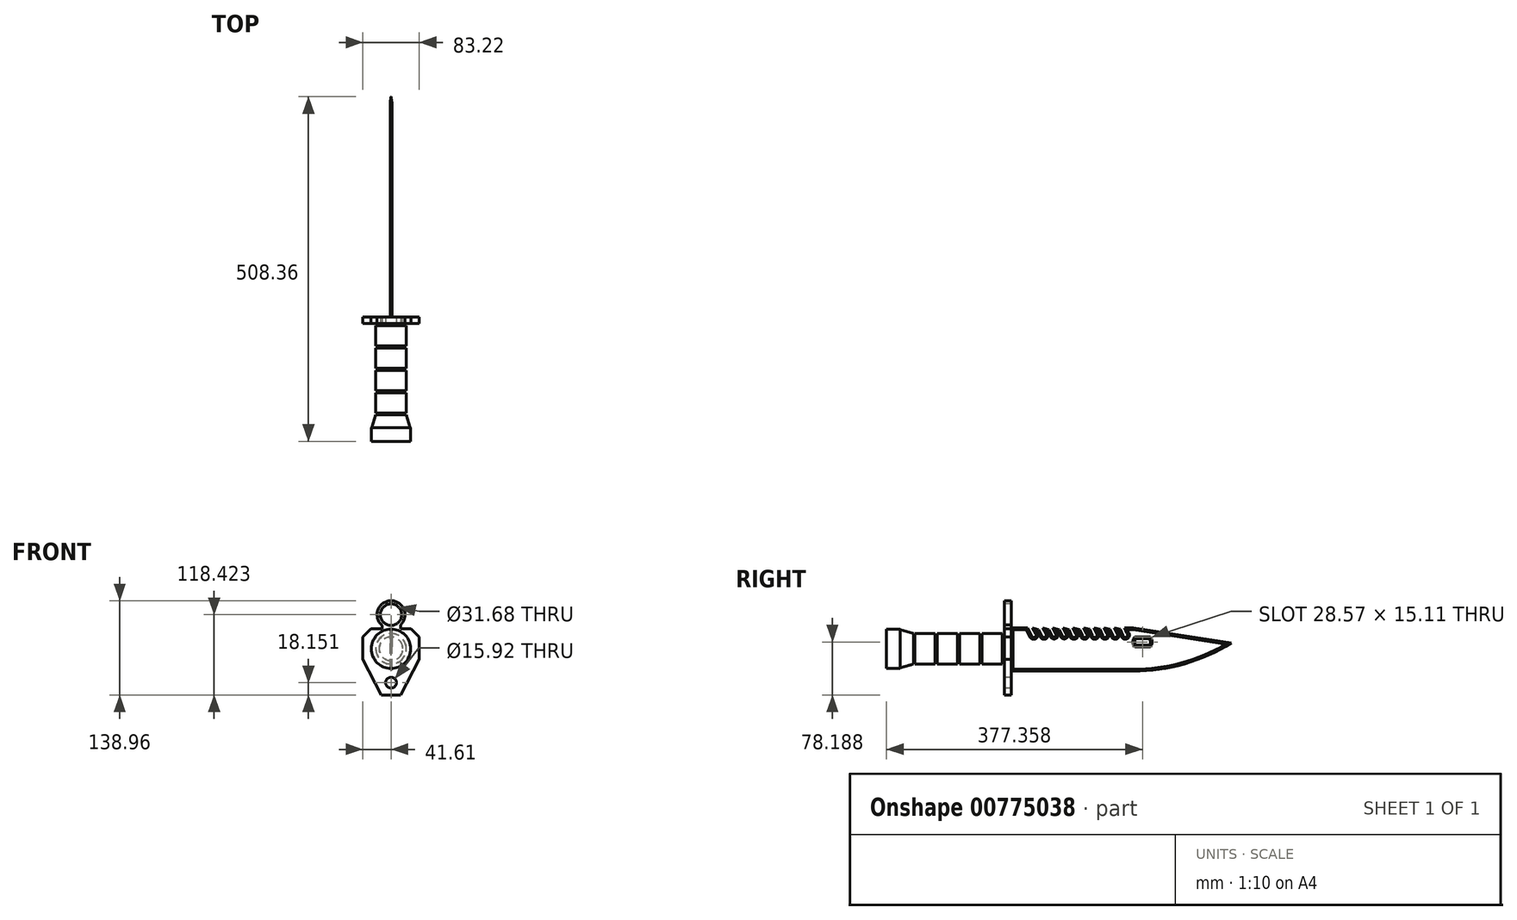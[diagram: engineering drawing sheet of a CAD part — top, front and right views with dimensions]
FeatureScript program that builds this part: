
annotation { "Feature Type Name" : "Feature", "Feature Type Description" : "" }
export const myFeature = defineFeature(function(context is Context, id is Id, definition is map)
    precondition{}
    {
        {
            var Q0;
            Q0=qCreatedBy(makeId("Right.planeOp"),FACE);
            var sketch = newSketch(context, id + "F0", { "sketchPlane" : qUnion([Q0])});
            skLineSegment(sketch, "E0", {"start": v(0, 0) * mm, "end": v(0, 17.36) * mm});
            skLineSegment(sketch, "E1", {"start": v(0, 17.36) * mm, "end": v(-3, 17.36) * mm});
            skLineSegment(sketch, "E2", {"start": v(-3, 17.36) * mm, "end": v(-3, 22.36) * mm});
            skLineSegment(sketch, "E3", {"start": v(-3, 22.36) * mm, "end": v(-33, 22.36) * mm});
            skLineSegment(sketch, "E4", {"start": v(-33, 22.36) * mm, "end": v(-33, 17.36) * mm});
            skLineSegment(sketch, "E5", {"start": v(-33, 17.36) * mm, "end": v(-36, 17.36) * mm});
            skLineSegment(sketch, "E6", {"start": v(-36, 17.36) * mm, "end": v(-36, 22.36) * mm});
            skLineSegment(sketch, "E7", {"start": v(-36, 22.36) * mm, "end": v(-66, 22.36) * mm});
            skLineSegment(sketch, "E8", {"start": v(-66, 22.36) * mm, "end": v(-66, 17.36) * mm});
            skLineSegment(sketch, "E9", {"start": v(-66, 17.36) * mm, "end": v(-69, 17.36) * mm});
            skLineSegment(sketch, "E10", {"start": v(-69, 17.36) * mm, "end": v(-69, 22.36) * mm});
            skLineSegment(sketch, "E11", {"start": v(-69, 22.36) * mm, "end": v(-99, 22.36) * mm});
            skLineSegment(sketch, "E12", {"start": v(-99, 22.36) * mm, "end": v(-99, 17.36) * mm});
            skLineSegment(sketch, "E13", {"start": v(-99, 17.36) * mm, "end": v(-102, 17.36) * mm});
            skLineSegment(sketch, "E14", {"start": v(-102, 17.36) * mm, "end": v(-102, 22.36) * mm});
            skLineSegment(sketch, "E15", {"start": v(-102, 22.36) * mm, "end": v(-132, 22.36) * mm});
            skLineSegment(sketch, "E16", {"start": v(-132, 22.36) * mm, "end": v(-132, 17.64) * mm});
            skLineSegment(sketch, "E17", {"start": v(-132, 17.64) * mm, "end": v(-134, 17.64) * mm});
            skLineSegment(sketch, "E18", {"start": v(-134, 17.64) * mm, "end": v(-134, 22.64) * mm});
            skLineSegment(sketch, "E19", {"start": v(-134, 22.64) * mm, "end": v(-153.56, 28.06) * mm});
            skLineSegment(sketch, "E20", {"start": v(-153.56, 28.06) * mm, "end": v(-153.56, 29.06) * mm});
            skLineSegment(sketch, "E21", {"start": v(-153.56, 29.06) * mm, "end": v(-173.56, 29.06) * mm});
            skLineSegment(sketch, "E22", {"start": v(-173.56, 29.06) * mm, "end": v(-173.56, 0) * mm});
            skLineSegment(sketch, "E23", {"start": v(-173.56, 0) * mm, "end": v(0, 0) * mm});
            skSolve(sketch);
        }
        {
            var Q0;
            Q0=qSketchRegion(id+"F0",true);
            var Q1;
            Q1=sQuery(id+"F0.wireOp",EDGE,"E23");
            revolve(context, id + "F1", {"entities" : qUnion([Q0]), "axis" : qUnion([Q1]), "revolveType" : RevolveType.FULL});
        }
        {
            var Q0;
            Q0=qCreatedBy(makeId("Front.planeOp"),FACE);
            var sketch = newSketch(context, id + "F2", { "sketchPlane" : qUnion([Q0])});
            skLineSegment(sketch, "E24", {"start": v(0, -68.1) * mm, "end": v(14.11, -68.1) * mm});
            skLineSegment(sketch, "E25", {"start": v(14.11, -68.1) * mm, "end": v(41.6, -15.3) * mm});
            skLineSegment(sketch, "E26", {"start": v(41.6, -15.3) * mm, "end": v(41.6, 17.5) * mm});
            skLineSegment(sketch, "E27", {"start": v(0, 29.79) * mm, "end": v(29.7, 29.79) * mm});
            skLineSegment(sketch, "E28", {"start": v(29.7, 29.79) * mm, "end": v(41.6, 17.5) * mm});
            skLineSegment(sketch, "E29.MirrorCS", {"start": v(-41.6, -15.3) * mm, "end": v(-41.6, 17.5) * mm});
            skLineSegment(sketch, "E30.MirrorCS", {"start": v(0, 29.79) * mm, "end": v(-29.7, 29.79) * mm});
            skLineSegment(sketch, "E31.MirrorCS", {"start": v(0, -68.1) * mm, "end": v(-14.11, -68.1) * mm});
            skLineSegment(sketch, "E32.MirrorCS", {"start": v(-14.11, -68.1) * mm, "end": v(-41.6, -15.3) * mm});
            skLineSegment(sketch, "E33.MirrorCS", {"start": v(-29.7, 29.79) * mm, "end": v(-41.6, 17.5) * mm});
            skCircle(sketch, "E34", {"center": v(0, -49.95) * mm, "radius": 7.96 * mm});
            skCircle(sketch, "E35", {"center": v(0, 50.32) * mm, "radius": 20.54 * mm});
            skCircle(sketch, "E36", {"center": v(0, 50.32) * mm, "radius": 15.84 * mm});
            skLineSegment(sketch, "E37", {"start": v(14.21, 35.5) * mm, "end": v(14.21, 29.79) * mm});
            skLineSegment(sketch, "E38", {"start": v(-13.2, 29.79) * mm, "end": v(-13.2, 34.59) * mm});
            skSolve(sketch);
        }
        {
            var Q0;
            Q0=qSketchRegion(id+"F2",true);
            extrude(context, id + "F3", {"entities" : qUnion([Q0]), "operationType" : NewBodyOperationType.ADD, "oppositeDirection" : true, "depth" : 10 * mm});
        }
        {
            var Q0;
            Q0=qCreatedBy(makeId("Right.planeOp"),FACE);
            var sketch = newSketch(context, id + "F4", { "sketchPlane" : qUnion([Q0])});
            skLineSegment(sketch, "E39", {"start": v(0, 0) * mm, "end": v(0, 30.7) * mm});
            skLineSegment(sketch, "E40", {"start": v(10.33, 30.7) * mm, "end": v(190.33, 30.7) * mm});
            skLineSegment(sketch, "E41", {"start": v(190.33, 30.7) * mm, "end": v(334.8, 8.42) * mm});
            skLineSegment(sketch, "E42", {"start": v(10.33, -32.89) * mm, "end": v(190.33, -32.89) * mm});
            skArc(sketch, "E43", {"start": v(190.33, -32.89) * mm, "mid": v(265.46, -22.36) * mm, "end": v(334.8, 8.42) * mm});
            skCircle(sketch, "E44", {"center": v(43.38, 20.17) * mm, "radius": 3.5 * mm});
            skLineSegment(sketch, "E45", {"start": v(41.53, 30.7) * mm, "end": v(47.34, 20.24) * mm});
            skLineSegment(sketch, "E46", {"start": v(34.52, 30.7) * mm, "end": v(41.24, 16.49) * mm});
            skCircle(sketch, "E47", {"center": v(58.38, 20.17) * mm, "radius": 3.5 * mm});
            skLineSegment(sketch, "E48", {"start": v(56.53, 30.7) * mm, "end": v(62.34, 20.23) * mm});
            skLineSegment(sketch, "E49", {"start": v(10.33, 30.7) * mm, "end": v(10.33, -32.89) * mm});
            skLineSegment(sketch, "E50", {"start": v(55.4, 18.32) * mm, "end": v(49.52, 30.7) * mm});
            skLineSegment(sketch, "E51", {"start": v(41.53, 30.7) * mm, "end": v(50.56, 28.52) * mm});
            skCircle(sketch, "E52", {"center": v(73.38, 20.17) * mm, "radius": 3.02 * mm});
            skLineSegment(sketch, "E53", {"start": v(64.52, 30.7) * mm, "end": v(71.98, 16.29) * mm});
            skLineSegment(sketch, "E54", {"start": v(71.53, 30.7) * mm, "end": v(77.13, 19.4) * mm});
            skLineSegment(sketch, "E55", {"start": v(56.53, 30.7) * mm, "end": v(65.66, 28.52) * mm});
            skCircle(sketch, "E56", {"center": v(88.38, 20.17) * mm, "radius": 3 * mm});
            skLineSegment(sketch, "E57", {"start": v(85.71, 18.8) * mm, "end": v(79.52, 30.7) * mm});
            skLineSegment(sketch, "E58", {"start": v(64.52, 30.7) * mm, "end": v(79.52, 30.7) * mm});
            skLineSegment(sketch, "E59", {"start": v(71.53, 30.7) * mm, "end": v(80.66, 28.52) * mm});
            skLineSegment(sketch, "E60", {"start": v(91.21, 21.13) * mm, "end": v(86.53, 30.7) * mm});
            skCircle(sketch, "E61", {"center": v(102.57, 20.17) * mm, "radius": 3.5 * mm});
            skLineSegment(sketch, "E62", {"start": v(99.3, 18.91) * mm, "end": v(94.77, 30.7) * mm});
            skLineSegment(sketch, "E63", {"start": v(106.07, 20.24) * mm, "end": v(101.13, 30.7) * mm});
            skLineSegment(sketch, "E64", {"start": v(86.53, 30.7) * mm, "end": v(95.61, 28.52) * mm});
            skCircle(sketch, "E65", {"center": v(118.43, 20.17) * mm, "radius": 3.5 * mm});
            skLineSegment(sketch, "E66", {"start": v(114.93, 20.24) * mm, "end": v(109.99, 30.7) * mm});
            skLineSegment(sketch, "E67", {"start": v(109.99, 30.7) * mm, "end": v(101.13, 30.7) * mm});
            skLineSegment(sketch, "E68", {"start": v(111.02, 28.52) * mm, "end": v(101.13, 30.7) * mm});
            skLineSegment(sketch, "E69", {"start": v(121.93, 20.24) * mm, "end": v(116.98, 30.7) * mm});
            skCircle(sketch, "E70", {"center": v(133.43, 20.17) * mm, "radius": 3.5 * mm});
            skLineSegment(sketch, "E71", {"start": v(129.93, 20.24) * mm, "end": v(124.99, 30.7) * mm});
            skLineSegment(sketch, "E72", {"start": v(124.99, 30.7) * mm, "end": v(132.31, 30.7) * mm});
            skLineSegment(sketch, "E73", {"start": v(136.93, 20.24) * mm, "end": v(131.98, 30.7) * mm});
            skLineSegment(sketch, "E74", {"start": v(116.98, 30.7) * mm, "end": v(125.92, 28.73) * mm});
            skCircle(sketch, "E75", {"center": v(148.43, 20.24) * mm, "radius": 3.5 * mm});
            skLineSegment(sketch, "E76", {"start": v(144.93, 20.17) * mm, "end": v(139.95, 30.7) * mm});
            skLineSegment(sketch, "E77", {"start": v(140.88, 28.73) * mm, "end": v(132.31, 30.7) * mm});
            skLineSegment(sketch, "E78", {"start": v(151.93, 20.24) * mm, "end": v(146.99, 30.7) * mm});
            skCircle(sketch, "E79", {"center": v(163.43, 20.24) * mm, "radius": 3.5 * mm});
            skLineSegment(sketch, "E80", {"start": v(159.93, 20.17) * mm, "end": v(154.95, 30.7) * mm});
            skLineSegment(sketch, "E81", {"start": v(166.93, 20.24) * mm, "end": v(161.99, 30.7) * mm});
            skCircle(sketch, "E82", {"center": v(178.43, 20.24) * mm, "radius": 3.5 * mm});
            skLineSegment(sketch, "E83", {"start": v(174.93, 20.24) * mm, "end": v(169.99, 30.7) * mm});
            skLineSegment(sketch, "E84", {"start": v(181.93, 20.24) * mm, "end": v(176.99, 30.7) * mm});
            skLineSegment(sketch, "E85", {"start": v(161.99, 30.7) * mm, "end": v(170.96, 28.64) * mm});
            skLineSegment(sketch, "E86", {"start": v(146.99, 30.7) * mm, "end": v(155.92, 28.64) * mm});
            skLineSegment(sketch, "E87", {"start": v(193.78, 14.96) * mm, "end": v(213.63, 14.96) * mm});
            skLineSegment(sketch, "E88", {"start": v(193.78, 5.21) * mm, "end": v(213.63, 5.21) * mm});
            skArc(sketch, "E89", {"start": v(193.78, 14.96) * mm, "mid": v(192.2, 10.09) * mm, "end": v(193.78, 5.21) * mm});
            skArc(sketch, "E90", {"start": v(213.63, 5.21) * mm, "mid": v(215.4, 10.09) * mm, "end": v(213.63, 14.96) * mm});
            skSolve(sketch);
        }
        {
            var Q0;
            {var subQ66=sQuery(id+"F4.wireOp",EDGE,"E41");Q0=makeQuery(id+"F4.imprint","IMPRINT",FACE,{"disambiguationData":[TD([[makeQuery(id+"F4.imprint","IMPRINT",EDGE,{"derivedFrom":subQ66}),-1.0]])]});}
            extrude(context, id + "F5", {"entities" : qUnion([Q0]), "endBound" : BoundingType.SYMMETRIC, "depth" : 2.5 * mm, "hasDraft" : true, "draftAngle" : 65 * degree, "draftPullDirection" : true});
        }
    });
